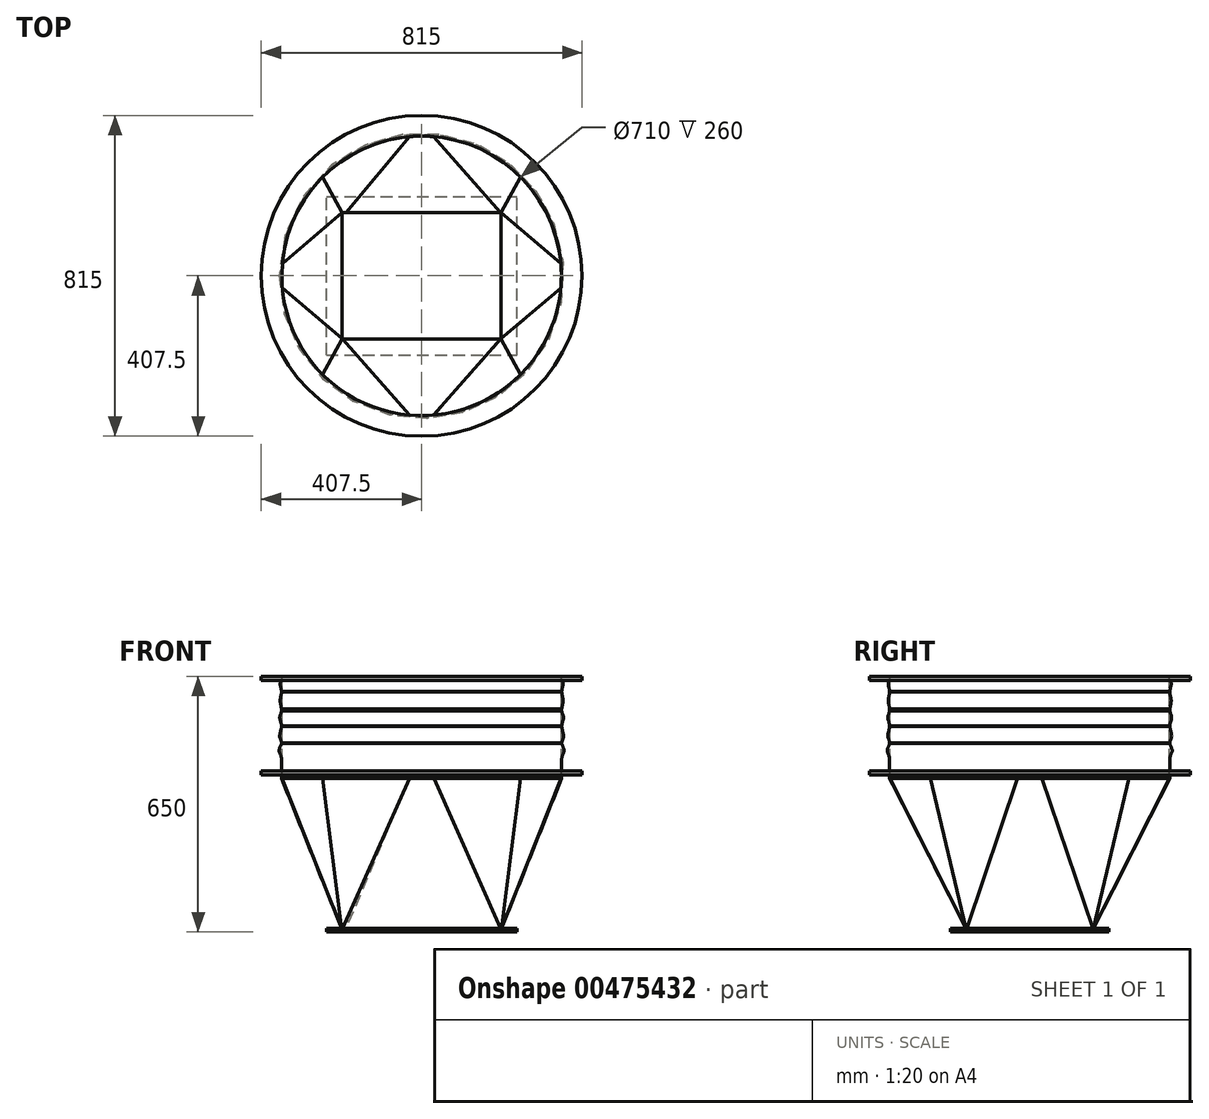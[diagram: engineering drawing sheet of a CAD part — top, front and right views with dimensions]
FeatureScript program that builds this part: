
annotation { "Feature Type Name" : "Feature", "Feature Type Description" : "" }
export const myFeature = defineFeature(function(context is Context, id is Id, definition is map)
    precondition{}
    {
        {
            var Q0;
            Q0=qCreatedBy(makeId("Front.planeOp"),FACE);
            var sketch = newSketch(context, id + "F0", { "sketchPlane" : qUnion([Q0])});
            skLineSegment(sketch, "E0", {"start": v(0, 359.58) * mm, "end": v(0, -1055.76) * mm, "construction": true});
            skLineSegment(sketch, "E1", {"start": v(-355, 48.38) * mm, "end": v(-355, 98.38) * mm});
            skLineSegment(sketch, "E2", {"start": v(-356, 98.38) * mm, "end": v(-356, 48.38) * mm});
            skLineSegment(sketch, "E3", {"start": v(-356, 48.38) * mm, "end": v(-355, 48.38) * mm});
            skLineSegment(sketch, "E4", {"start": v(-356, 98.38) * mm, "end": v(-355, 98.38) * mm});
            skLineSegment(sketch, "E5.bottom", {"start": v(-356, 58.38) * mm, "end": v(-407.5, 58.38) * mm});
            skLineSegment(sketch, "E5.top", {"start": v(-356, 68.38) * mm, "end": v(-407.5, 68.38) * mm});
            skLineSegment(sketch, "E5.left", {"start": v(-356, 58.38) * mm, "end": v(-356, 68.38) * mm});
            skLineSegment(sketch, "E5.right", {"start": v(-407.5, 58.38) * mm, "end": v(-407.5, 68.38) * mm});
            skSolve(sketch);
        }
        {
            var Q0;
            Q0=makeQuery(id+"F0.imprint","IMPRINT",FACE,{"disambiguationData":[TD([[makeQuery(id+"F0.imprint","IMPRINT",EDGE,{"derivedFrom":sQuery(id+"F0.wireOp",EDGE,"E1")}),1.0]])]});
            var Q1;
            Q1=makeQuery(id+"F0.imprint","IMPRINT",FACE,{"disambiguationData":[TD([[makeQuery(id+"F0.imprint","IMPRINT",EDGE,{"derivedFrom":sQuery(id+"F0.wireOp",EDGE,"E5.bottom")}),-1.0]])]});
            var Q2;
            Q2=sQuery(id+"F0.wireOp",EDGE,"E0");
            revolve(context, id + "F1", {"entities" : qUnion([Q0, Q1]), "axis" : qUnion([Q2]), "revolveType" : RevolveType.FULL});
        }
        {
            var Q0;
            Q0=makeQuery(id+"F1.opRevolve","SWEPT_FACE",FACE,{"disambiguationData":[OSD([sQuery(id+"F0.wireOp",EDGE,"E3")])]});
            cPlane(context, id + "F2", {"entities" : qUnion([Q0]), "cplaneType" : CPlaneType.OFFSET, "offset" : 390 * mm, "width" : 150 * mm, "height" : 150 * mm});
        }
        {
            var Q0;
            Q0=qCreatedBy(id+"F2.planeOp",FACE);
            var sketch = newSketch(context, id + "F3", { "sketchPlane" : qUnion([Q0])});
            skLineSegment(sketch, "E6", {"start": v(-444.7, 0) * mm, "end": v(477.26, 0) * mm, "construction": true});
            skLineSegment(sketch, "E7", {"start": v(0, -623.33) * mm, "end": v(0, 662) * mm, "construction": true});
            skLineSegment(sketch, "E8.bottom", {"start": v(-202, 161) * mm, "end": v(202, 161) * mm});
            skLineSegment(sketch, "E8.top", {"start": v(-202, -161) * mm, "end": v(202, -161) * mm});
            skLineSegment(sketch, "E8.left", {"start": v(-202, 161) * mm, "end": v(-202, -161) * mm});
            skLineSegment(sketch, "E8.right", {"start": v(202, 161) * mm, "end": v(202, -161) * mm});
            skPoint(sketch, "E8.middle", {"position": v(0, 0) * mm});
            skLineSegment(sketch, "E9.bottom", {"start": v(-242, 201) * mm, "end": v(242, 201) * mm});
            skLineSegment(sketch, "E9.top", {"start": v(-242, -201) * mm, "end": v(242, -201) * mm});
            skLineSegment(sketch, "E9.left", {"start": v(-242, 201) * mm, "end": v(-242, -201) * mm});
            skLineSegment(sketch, "E9.right", {"start": v(242, 201) * mm, "end": v(242, -201) * mm});
            skSolve(sketch);
        }
        {
            var Q0;
            Q0=makeQuery(id+"F3.imprint","IMPRINT",FACE,{"disambiguationData":[TD([[makeQuery(id+"F3.imprint","IMPRINT",EDGE,{"derivedFrom":sQuery(id+"F3.wireOp",EDGE,"E8.bottom")}),1.0]])]});
            extrude(context, id + "F4", {"entities" : qUnion([Q0]), "oppositeDirection" : true, "depth" : 10 * mm});
        }
        {
            var Q0;
            Q0=makeQuery(id+"F1.opRevolve","SWEPT_FACE",FACE,{"disambiguationData":[OSD([sQuery(id+"F0.wireOp",EDGE,"E3")])]});
            var sketch = newSketch(context, id + "F5", { "sketchPlane" : qUnion([Q0])});
            skLineSegment(sketch, "E10", {"start": v(0, 0) * mm, "end": v(0, -455.71) * mm, "construction": true});
            skLineSegment(sketch, "E11", {"start": v(0, 0) * mm, "end": v(-39.8, -454.85) * mm, "construction": true});
            skLineSegment(sketch, "E12", {"start": v(0, 0) * mm, "end": v(-439.86, -38.48) * mm, "construction": true});
            skLineSegment(sketch, "E13", {"start": v(-31.03, -354.65) * mm, "end": v(-30.94, -353.65) * mm});
            skLineSegment(sketch, "E14", {"start": v(-354.65, -31.03) * mm, "end": v(-353.65, -30.94) * mm});
            skLineSegment(sketch, "E15", {"start": v(0, 0) * mm, "end": v(-315.48, -315.48) * mm, "construction": true});
            skArc(sketch, "E16", {"start": v(-30.94, -353.65) * mm, "mid": v(-150.03, -321.74) * mm, "end": v(-251.02, -251.02) * mm});
            skArc(sketch, "E17", {"start": v(-251.02, -251.02) * mm, "mid": v(-321.74, -150.03) * mm, "end": v(-353.65, -30.94) * mm});
            skArc(sketch, "E18", {"start": v(-354.65, -31.03) * mm, "mid": v(-322.65, -150.45) * mm, "end": v(-251.73, -251.73) * mm});
            skArc(sketch, "E19", {"start": v(-251.73, -251.73) * mm, "mid": v(-150.45, -322.65) * mm, "end": v(-31.03, -354.65) * mm});
            skArc(sketch, "E20", {"start": v(30.5, -348.67) * mm, "mid": v(0, -350) * mm, "end": v(-30.5, -348.67) * mm});
            skArc(sketch, "E21", {"start": v(31.03, -354.65) * mm, "mid": v(0, -356) * mm, "end": v(-31.03, -354.65) * mm});
            skLineSegment(sketch, "E22.anchor1", {"start": v(0.06, 0.65) * mm, "end": v(-31.03, -354.65) * mm, "construction": true});
            skLineSegment(sketch, "E23", {"start": v(0, 0) * mm, "end": v(39.51, -451.6) * mm, "construction": true});
            skLineSegment(sketch, "E24", {"start": v(31.03, -354.65) * mm, "end": v(30.5, -348.67) * mm});
            skLineSegment(sketch, "E25.1.0", {"start": v(0, 0) * mm, "end": v(-454.85, 39.8) * mm, "construction": true});
            skLineSegment(sketch, "E25.1.1", {"start": v(0, 0) * mm, "end": v(-455.71, 0) * mm, "construction": true});
            skLineSegment(sketch, "E25.1.2", {"start": v(0, 0) * mm, "end": v(-451.6, -39.51) * mm, "construction": true});
            skLineSegment(sketch, "E25.1.3", {"start": v(0, 0) * mm, "end": v(-38.48, 439.86) * mm, "construction": true});
            skLineSegment(sketch, "E25.1.4", {"start": v(0, 0) * mm, "end": v(-315.48, 315.48) * mm, "construction": true});
            skArc(sketch, "E25.1.5", {"start": v(-251.73, 251.73) * mm, "mid": v(-322.65, 150.45) * mm, "end": v(-354.65, 31.03) * mm});
            skArc(sketch, "E25.1.6", {"start": v(-31.03, 354.65) * mm, "mid": v(-150.45, 322.65) * mm, "end": v(-251.73, 251.73) * mm});
            skLineSegment(sketch, "E25.1.7", {"start": v(0.65, -0.06) * mm, "end": v(-354.65, 31.03) * mm, "construction": true});
            skArc(sketch, "E25.1.8", {"start": v(-353.65, 30.94) * mm, "mid": v(-321.74, 150.03) * mm, "end": v(-251.02, 251.02) * mm});
            skArc(sketch, "E25.1.9", {"start": v(-251.02, 251.02) * mm, "mid": v(-150.03, 321.74) * mm, "end": v(-30.94, 353.65) * mm});
            skLineSegment(sketch, "E25.1.10", {"start": v(0, 0) * mm, "end": v(-315.48, 315.48) * mm, "construction": true});
            skLineSegment(sketch, "E25.1.11", {"start": v(-31.03, 354.65) * mm, "end": v(-30.94, 353.65) * mm});
            skArc(sketch, "E25.1.12", {"start": v(-354.65, -31.03) * mm, "mid": v(-356, 0) * mm, "end": v(-354.65, 31.03) * mm});
            skArc(sketch, "E25.1.13", {"start": v(-348.67, -30.5) * mm, "mid": v(-350, 0) * mm, "end": v(-348.67, 30.5) * mm});
            skLineSegment(sketch, "E25.1.14", {"start": v(-354.65, -31.03) * mm, "end": v(-348.67, -30.5) * mm});
            skLineSegment(sketch, "E25.1.15", {"start": v(-354.65, 31.03) * mm, "end": v(-353.65, 30.94) * mm});
            skLineSegment(sketch, "E25.2.0", {"start": v(0, 0) * mm, "end": v(39.8, 454.85) * mm, "construction": true});
            skLineSegment(sketch, "E25.2.1", {"start": v(0, 0) * mm, "end": v(0, 455.71) * mm, "construction": true});
            skLineSegment(sketch, "E25.2.2", {"start": v(0, 0) * mm, "end": v(-39.51, 451.6) * mm, "construction": true});
            skLineSegment(sketch, "E25.2.3", {"start": v(0, 0) * mm, "end": v(439.86, 38.48) * mm, "construction": true});
            skLineSegment(sketch, "E25.2.4", {"start": v(0, 0) * mm, "end": v(315.48, 315.48) * mm, "construction": true});
            skArc(sketch, "E25.2.5", {"start": v(251.73, 251.73) * mm, "mid": v(150.45, 322.65) * mm, "end": v(31.03, 354.65) * mm});
            skArc(sketch, "E25.2.6", {"start": v(354.65, 31.03) * mm, "mid": v(322.65, 150.45) * mm, "end": v(251.73, 251.73) * mm});
            skLineSegment(sketch, "E25.2.7", {"start": v(-0.06, -0.65) * mm, "end": v(31.03, 354.65) * mm, "construction": true});
            skArc(sketch, "E25.2.8", {"start": v(30.94, 353.65) * mm, "mid": v(150.03, 321.74) * mm, "end": v(251.02, 251.02) * mm});
            skArc(sketch, "E25.2.9", {"start": v(251.02, 251.02) * mm, "mid": v(321.74, 150.03) * mm, "end": v(353.65, 30.94) * mm});
            skLineSegment(sketch, "E25.2.10", {"start": v(0, 0) * mm, "end": v(315.48, 315.48) * mm, "construction": true});
            skLineSegment(sketch, "E25.2.11", {"start": v(354.65, 31.03) * mm, "end": v(353.65, 30.94) * mm});
            skArc(sketch, "E25.2.12", {"start": v(-31.03, 354.65) * mm, "mid": v(0, 356) * mm, "end": v(31.03, 354.65) * mm});
            skArc(sketch, "E25.2.13", {"start": v(-30.5, 348.67) * mm, "mid": v(0, 350) * mm, "end": v(30.5, 348.67) * mm});
            skLineSegment(sketch, "E25.2.14", {"start": v(-31.03, 354.65) * mm, "end": v(-30.5, 348.67) * mm});
            skLineSegment(sketch, "E25.2.15", {"start": v(31.03, 354.65) * mm, "end": v(30.94, 353.65) * mm});
            skLineSegment(sketch, "E25.3.0", {"start": v(0, 0) * mm, "end": v(454.85, -39.8) * mm, "construction": true});
            skLineSegment(sketch, "E25.3.1", {"start": v(0, 0) * mm, "end": v(455.71, 0) * mm, "construction": true});
            skLineSegment(sketch, "E25.3.2", {"start": v(0, 0) * mm, "end": v(451.6, 39.51) * mm, "construction": true});
            skLineSegment(sketch, "E25.3.3", {"start": v(0, 0) * mm, "end": v(38.48, -439.86) * mm, "construction": true});
            skLineSegment(sketch, "E25.3.4", {"start": v(0, 0) * mm, "end": v(315.48, -315.48) * mm, "construction": true});
            skArc(sketch, "E25.3.5", {"start": v(251.73, -251.73) * mm, "mid": v(322.65, -150.45) * mm, "end": v(354.65, -31.03) * mm});
            skArc(sketch, "E25.3.6", {"start": v(31.03, -354.65) * mm, "mid": v(150.45, -322.65) * mm, "end": v(251.73, -251.73) * mm});
            skLineSegment(sketch, "E25.3.7", {"start": v(-0.65, 0.06) * mm, "end": v(354.65, -31.03) * mm, "construction": true});
            skArc(sketch, "E25.3.8", {"start": v(353.65, -30.94) * mm, "mid": v(321.74, -150.03) * mm, "end": v(251.02, -251.02) * mm});
            skArc(sketch, "E25.3.9", {"start": v(251.02, -251.02) * mm, "mid": v(150.03, -321.74) * mm, "end": v(30.94, -353.65) * mm});
            skLineSegment(sketch, "E25.3.10", {"start": v(0, 0) * mm, "end": v(315.48, -315.48) * mm, "construction": true});
            skLineSegment(sketch, "E25.3.11", {"start": v(31.03, -354.65) * mm, "end": v(30.94, -353.65) * mm});
            skArc(sketch, "E25.3.12", {"start": v(354.65, 31.03) * mm, "mid": v(356, 0) * mm, "end": v(354.65, -31.03) * mm});
            skArc(sketch, "E25.3.13", {"start": v(348.67, 30.5) * mm, "mid": v(350, 0) * mm, "end": v(348.67, -30.5) * mm});
            skLineSegment(sketch, "E25.3.14", {"start": v(354.65, 31.03) * mm, "end": v(348.67, 30.5) * mm});
            skLineSegment(sketch, "E25.3.15", {"start": v(354.65, -31.03) * mm, "end": v(353.65, -30.94) * mm});
            skLineSegment(sketch, "E25.anchor2", {"start": v(0, 0) * mm, "end": v(315.48, -315.48) * mm, "construction": true});
            skSolve(sketch);
        }
        {
            var Q0;
            Q0=makeQuery(id+"F4.opExtrude","CAP_FACE",FACE,{"disambiguationData":[OSD([sQuery(id+"F3.wireOp",EDGE,"E8.bottom"),sQuery(id+"F3.wireOp",EDGE,"E8.top"),sQuery(id+"F3.wireOp",EDGE,"E8.left"),sQuery(id+"F3.wireOp",EDGE,"E8.right"),sQuery(id+"F3.wireOp",EDGE,"E9.bottom"),sQuery(id+"F3.wireOp",EDGE,"E9.top"),sQuery(id+"F3.wireOp",EDGE,"E9.left"),sQuery(id+"F3.wireOp",EDGE,"E9.right")])],"isStart":false});
            var sketch = newSketch(context, id + "F6", { "sketchPlane" : qUnion([Q0])});
            skLineSegment(sketch, "E26.bottom", {"start": v(-202, 161) * mm, "end": v(202, 161) * mm});
            skLineSegment(sketch, "E26.top", {"start": v(-202, -161) * mm, "end": v(202, -161) * mm});
            skLineSegment(sketch, "E26.left", {"start": v(-202, 161) * mm, "end": v(-202, -161) * mm});
            skLineSegment(sketch, "E26.right", {"start": v(202, 161) * mm, "end": v(202, -161) * mm});
            skPoint(sketch, "E26.middle", {"position": v(0, 0) * mm});
            skLineSegment(sketch, "E27.bottom", {"start": v(-203, 162) * mm, "end": v(203, 162) * mm});
            skLineSegment(sketch, "E27.top", {"start": v(-201, -162) * mm, "end": v(203, -162) * mm});
            skLineSegment(sketch, "E27.left", {"start": v(-203, 162) * mm, "end": v(-203, -160) * mm});
            skLineSegment(sketch, "E27.right", {"start": v(203, 162) * mm, "end": v(203, -162) * mm});
            skLineSegment(sketch, "E28", {"start": v(-192, 161) * mm, "end": v(-192, 162) * mm});
            skLineSegment(sketch, "E29", {"start": v(-202, 160) * mm, "end": v(-203, 160) * mm});
            skLineSegment(sketch, "E30", {"start": v(201, 162) * mm, "end": v(201, 161) * mm});
            skLineSegment(sketch, "E31", {"start": v(202, 160) * mm, "end": v(203, 160) * mm});
            skLineSegment(sketch, "E32", {"start": v(203, -160) * mm, "end": v(202, -160) * mm});
            skLineSegment(sketch, "E33", {"start": v(201, -161) * mm, "end": v(201, -162) * mm});
            skLineSegment(sketch, "E34", {"start": v(-202, -160) * mm, "end": v(-203, -160) * mm});
            skLineSegment(sketch, "E35", {"start": v(-201, -161) * mm, "end": v(-201, -162) * mm});
            skLineSegment(sketch, "E36", {"start": v(-201, -162) * mm, "end": v(-203, -162) * mm});
            skLineSegment(sketch, "E37", {"start": v(-203, -162) * mm, "end": v(-203, -160) * mm});
            skSolve(sketch);
        }
        {
            var Q1;
            {var subQ3=sQuery(id+"F6.wireOp",EDGE,"E32");Q1=makeQuery(id+"F6.imprint","IMPRINT",FACE,{"disambiguationData":[TD([[makeQuery(id+"F6.imprint","IMPRINT",EDGE,{"derivedFrom":subQ3}),1.0]])]});}
            var Q2;
            Q2=makeQuery(id+"F5.imprint","IMPRINT",FACE,{"disambiguationData":[TD([[makeQuery(id+"F5.imprint","IMPRINT",EDGE,{"derivedFrom":sQuery(id+"F5.wireOp",EDGE,"E25.2.5")}),-1.0]])]});
            loft(context, id + "F7", {"operationType" : NewBodyOperationType.ADD, "sheetProfilesArray" : [{ "sheetProfileEntities" : qUnion([Q1]) }, { "sheetProfileEntities" : qUnion([Q2]) }]});
        }
        {
            var Q1;
            {var subQ0=sQuery(id+"F6.wireOp",EDGE,"E31");Q1=makeQuery(id+"F6.imprint","IMPRINT",FACE,{"disambiguationData":[TD([[makeQuery(id+"F6.imprint","IMPRINT",EDGE,{"derivedFrom":subQ0}),-1.0]])]});}
            var Q2;
            Q2=makeQuery(id+"F5.imprint","IMPRINT",FACE,{"disambiguationData":[TD([[makeQuery(id+"F5.imprint","IMPRINT",EDGE,{"derivedFrom":sQuery(id+"F5.wireOp",EDGE,"E25.3.12")}),-1.0]])]});
            loft(context, id + "F8", {"operationType" : NewBodyOperationType.ADD, "sheetProfilesArray" : [{ "sheetProfileEntities" : qUnion([Q1]) }, { "sheetProfileEntities" : qUnion([Q2]) }]});
        }
        {
            var Q1;
            {var subQ4=sQuery(id+"F6.wireOp",EDGE,"E30");Q1=makeQuery(id+"F6.imprint","IMPRINT",FACE,{"disambiguationData":[TD([[makeQuery(id+"F6.imprint","IMPRINT",EDGE,{"derivedFrom":subQ4}),1.0]])]});}
            var Q2;
            Q2=makeQuery(id+"F5.imprint","IMPRINT",FACE,{"disambiguationData":[TD([[makeQuery(id+"F5.imprint","IMPRINT",EDGE,{"derivedFrom":sQuery(id+"F5.wireOp",EDGE,"E25.3.5")}),-1.0]])]});
            loft(context, id + "F9", {"operationType" : NewBodyOperationType.ADD, "sheetProfilesArray" : [{ "sheetProfileEntities" : qUnion([Q1]) }, { "sheetProfileEntities" : qUnion([Q2]) }]});
        }
        {
            var Q1;
            {var subQ0=sQuery(id+"F6.wireOp",EDGE,"E33");Q1=makeQuery(id+"F6.imprint","IMPRINT",FACE,{"disambiguationData":[TD([[makeQuery(id+"F6.imprint","IMPRINT",EDGE,{"derivedFrom":subQ0}),-1.0]])]});}
            var Q2;
            Q2=makeQuery(id+"F5.imprint","IMPRINT",FACE,{"disambiguationData":[TD([[makeQuery(id+"F5.imprint","IMPRINT",EDGE,{"derivedFrom":sQuery(id+"F5.wireOp",EDGE,"E25.2.12")}),-1.0]])]});
            loft(context, id + "F10", {"operationType" : NewBodyOperationType.ADD, "sheetProfilesArray" : [{ "sheetProfileEntities" : qUnion([Q1]) }, { "sheetProfileEntities" : qUnion([Q2]) }]});
        }
        {
            var Q1;
            {var subQ4=sQuery(id+"F6.wireOp",EDGE,"E34");Q1=makeQuery(id+"F6.imprint","IMPRINT",FACE,{"disambiguationData":[TD([[makeQuery(id+"F6.imprint","IMPRINT",EDGE,{"derivedFrom":subQ4}),1.0]])]});}
            var Q2;
            Q2=makeQuery(id+"F5.imprint","IMPRINT",FACE,{"disambiguationData":[TD([[makeQuery(id+"F5.imprint","IMPRINT",EDGE,{"derivedFrom":sQuery(id+"F5.wireOp",EDGE,"E25.1.5")}),-1.0]])]});
            loft(context, id + "F11", {"operationType" : NewBodyOperationType.ADD, "sheetProfilesArray" : [{ "sheetProfileEntities" : qUnion([Q1]) }, { "sheetProfileEntities" : qUnion([Q2]) }]});
        }
        {
            var Q1;
            {var subQ0=sQuery(id+"F6.wireOp",EDGE,"E29");Q1=makeQuery(id+"F6.imprint","IMPRINT",FACE,{"disambiguationData":[TD([[makeQuery(id+"F6.imprint","IMPRINT",EDGE,{"derivedFrom":subQ0}),1.0]])]});}
            var Q2;
            Q2=makeQuery(id+"F5.imprint","IMPRINT",FACE,{"disambiguationData":[TD([[makeQuery(id+"F5.imprint","IMPRINT",EDGE,{"derivedFrom":sQuery(id+"F5.wireOp",EDGE,"E25.1.12")}),-1.0]])]});
            loft(context, id + "F12", {"operationType" : NewBodyOperationType.ADD, "sheetProfilesArray" : [{ "sheetProfileEntities" : qUnion([Q1]) }, { "sheetProfileEntities" : qUnion([Q2]) }]});
        }
        {
            var Q1;
            Q1=makeQuery(id+"F5.imprint","IMPRINT",FACE,{"disambiguationData":[TD([[makeQuery(id+"F5.imprint","IMPRINT",EDGE,{"derivedFrom":sQuery(id+"F5.wireOp",EDGE,"E13")}),1.0]])]});
            var Q2;
            {var subQ4=sQuery(id+"F6.wireOp",EDGE,"E28");Q2=makeQuery(id+"F6.imprint","IMPRINT",FACE,{"disambiguationData":[TD([[makeQuery(id+"F6.imprint","IMPRINT",EDGE,{"derivedFrom":subQ4}),1.0]])]});}
            loft(context, id + "F13", {"operationType" : NewBodyOperationType.ADD, "sheetProfilesArray" : [{ "sheetProfileEntities" : qUnion([Q1]) }, { "sheetProfileEntities" : qUnion([Q2]) }]});
        }
        {
            var Q1;
            Q1=makeQuery(id+"F5.imprint","IMPRINT",FACE,{"disambiguationData":[TD([[makeQuery(id+"F5.imprint","IMPRINT",EDGE,{"derivedFrom":sQuery(id+"F5.wireOp",EDGE,"E13")}),-1.0]])]});
            var Q2;
            {var subQ0=sQuery(id+"F6.wireOp",EDGE,"E28");Q2=makeQuery(id+"F6.imprint","IMPRINT",FACE,{"disambiguationData":[TD([[makeQuery(id+"F6.imprint","IMPRINT",EDGE,{"derivedFrom":subQ0}),-1.0]])]});}
            loft(context, id + "F14", {"operationType" : NewBodyOperationType.ADD, "sheetProfilesArray" : [{ "sheetProfileEntities" : qUnion([Q1]) }, { "sheetProfileEntities" : qUnion([Q2]) }]});
        }
        {
            var Q0;
            Q0=qCreatedBy(makeId("Front.planeOp"),FACE);
            var sketch = newSketch(context, id + "F15", { "sketchPlane" : qUnion([Q0])});
            skLineSegment(sketch, "E38", {"start": v(356, 98.38) * mm, "end": v(356, -51.62) * mm, "construction": true});
            skLineSegment(sketch, "E39", {"start": v(356, 98.38) * mm, "end": v(356, 588.27) * mm, "construction": true});
            skLineSegment(sketch, "E40", {"start": v(0, 0) * mm, "end": v(0, 686.8) * mm, "construction": true});
            skLineSegment(sketch, "E41.left", {"start": v(-356, 98.38) * mm, "end": v(-356, 298.38) * mm});
            skLineSegment(sketch, "E41.right", {"start": v(-355, 98.38) * mm, "end": v(-355, 298.38) * mm});
            skLineSegment(sketch, "E42.bottom", {"start": v(-356, 298.38) * mm, "end": v(-407.5, 298.38) * mm});
            skLineSegment(sketch, "E42.top", {"start": v(-355, 308.38) * mm, "end": v(-407.5, 308.38) * mm});
            skLineSegment(sketch, "E42.left", {"start": v(-355, 298.38) * mm, "end": v(-355, 308.38) * mm});
            skLineSegment(sketch, "E42.right", {"start": v(-407.5, 298.38) * mm, "end": v(-407.5, 308.38) * mm});
            skLineSegment(sketch, "E43", {"start": v(-356, 98.38) * mm, "end": v(-355, 98.38) * mm});
            skFitSpline(sketch, "E44", {"points": [v(-356, 298.38) * mm, v(-359.54, 289.48) * mm, v(-356, 269.32) * mm, v(-359.31, 246.43) * mm, v(-356, 220.65) * mm, v(-360.53, 203.96) * mm, v(-356, 182.12) * mm, v(-360.53, 155.43) * mm, v(-356, 138.14) * mm, v(-362.04, 119.94) * mm, v(-356, 99.31) * mm], "startDerivative": vector(-75.53, -113.74) * mm, "endDerivative": vector(0, -234.8) * mm});
            skSolve(sketch);
        }
        {
            var Q0;
            Q0=qSketchRegion(id+"F15",true);
            var Q1;
            Q1=sQuery(id+"F15.wireOp",EDGE,"E40");
            revolve(context, id + "F16", {"operationType" : NewBodyOperationType.ADD, "entities" : qUnion([Q0]), "axis" : qUnion([Q1]), "revolveType" : RevolveType.FULL});
        }
    });
